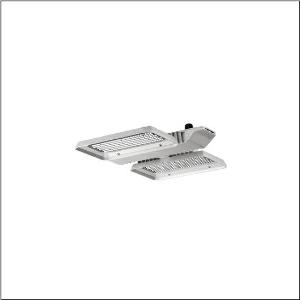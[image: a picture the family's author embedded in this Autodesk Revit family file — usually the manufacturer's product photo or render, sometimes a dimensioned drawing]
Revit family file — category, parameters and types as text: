
# Revit family: highbay_11_51hl61d14dca
name_source: partatom
category: Lighting Fixtures
units: mm (PartAtom-declared; Revit-internal decimal feet)

## family parameters
Cut with Voids When Loaded = No
Host = Face
Light Source = No
Part Type = Normal
Room Calculation Point = No
Round Connector Dimension = Use Diameter
Shared = No

## types (1)
- --- (1 x LED, 9790 lm, 55.6 W, 4000K)
    Apparent Load = 56 VA
    CIE Flux Codes = 88 95 99 100 99
    Color Rendering = 80
    Color Temperature = 4000K
    Default Elevation = 1800 mm
    Description = Highbay 11, LED high bay luminaire, primary light control with lens, of PMMA, light emission: direct distribution, primary light characteristic: symmetric, installation type: surface-mounted, suspended mounting, for 1x 2x LED, rated luminous flux: 9.790lm, luminous efficacy: 176lm/W, light colour: 840, colour temperature: 4000K, control gear: ECG DALI, with terminal, 5-pole, max. 2.5mm², mains connection: 230..240V, AC, 50/60Hz, rated input power: 56W, LED unit, of diecast aluminium, coated, metallic grey (RAL 9006), length: 470mm, width: 500mm, height: 65mm, housing, of diecast aluminium, coated, metallic grey (RAL 9006), protection rating (complete): IP65, insulation class (complete): insulation class I (protective earthing), certification: CE, ENEC, VDE, UKCA, protection symbol: D, impact resistance: IK08 with glass or PC cover, permissible operating ambient temperature: -35..+70°C, corresponds to IFS (International Featured Standards) requirements for safety and quality in the food industry, reducing of maximum allowable ambient temperature of 5°C with ceiling mounting, packaging unit: 1 piece
    Height = 95 mm
    Lamp = 1 x LED
    Lamp Light Flux = 9790 lm
    Lamp Power = 55.6 W
    Lamp count = 1
    Length = 468 mm
    Luminous efficacy = 176 lm/W
    Manufacturer = Siteco
    ModVariant = No
    Model = 51HL61D14DCA
    Mounting Place = Ceiling
    Mounting Type = Pendant
    Number of Poles = 1
    OnlyDefault = Yes
    Power Factor = 1
    Product Name = Highbay 11
    Product group = LED high bay luminaire
    ProductGroupID = 903
    Protection Class = Protection class I
    Protection Degree = IP 65
    RLX_Detail_Level = 1
    RLX_Emergency_Light_Flux = 0 lm
    RLX_Emergency_Type = 0
    RLX_Emergency_Type_DB = No
    RlxData = <blob elided: 70537 chars, md5=68626158>
    Socket = socket
    Standby Power = 0 W
    System Light Flux = 9790 lm
    System Power = 56 W
    Type Comments = factory setting: luminous flux: 100 % | dim-lin: 254 | 315 mA
    Type Image = l_1003425.jpg
    URL = http://relux.com
    VarID = @adj_177515
    Voltage = 0 V
    Weight = 0.00 kg
    Width = 501 mm

## geometry (parser evidence)
native form markers: Blend x4, Sweep x14
no freeform markers — native parametric forms only
